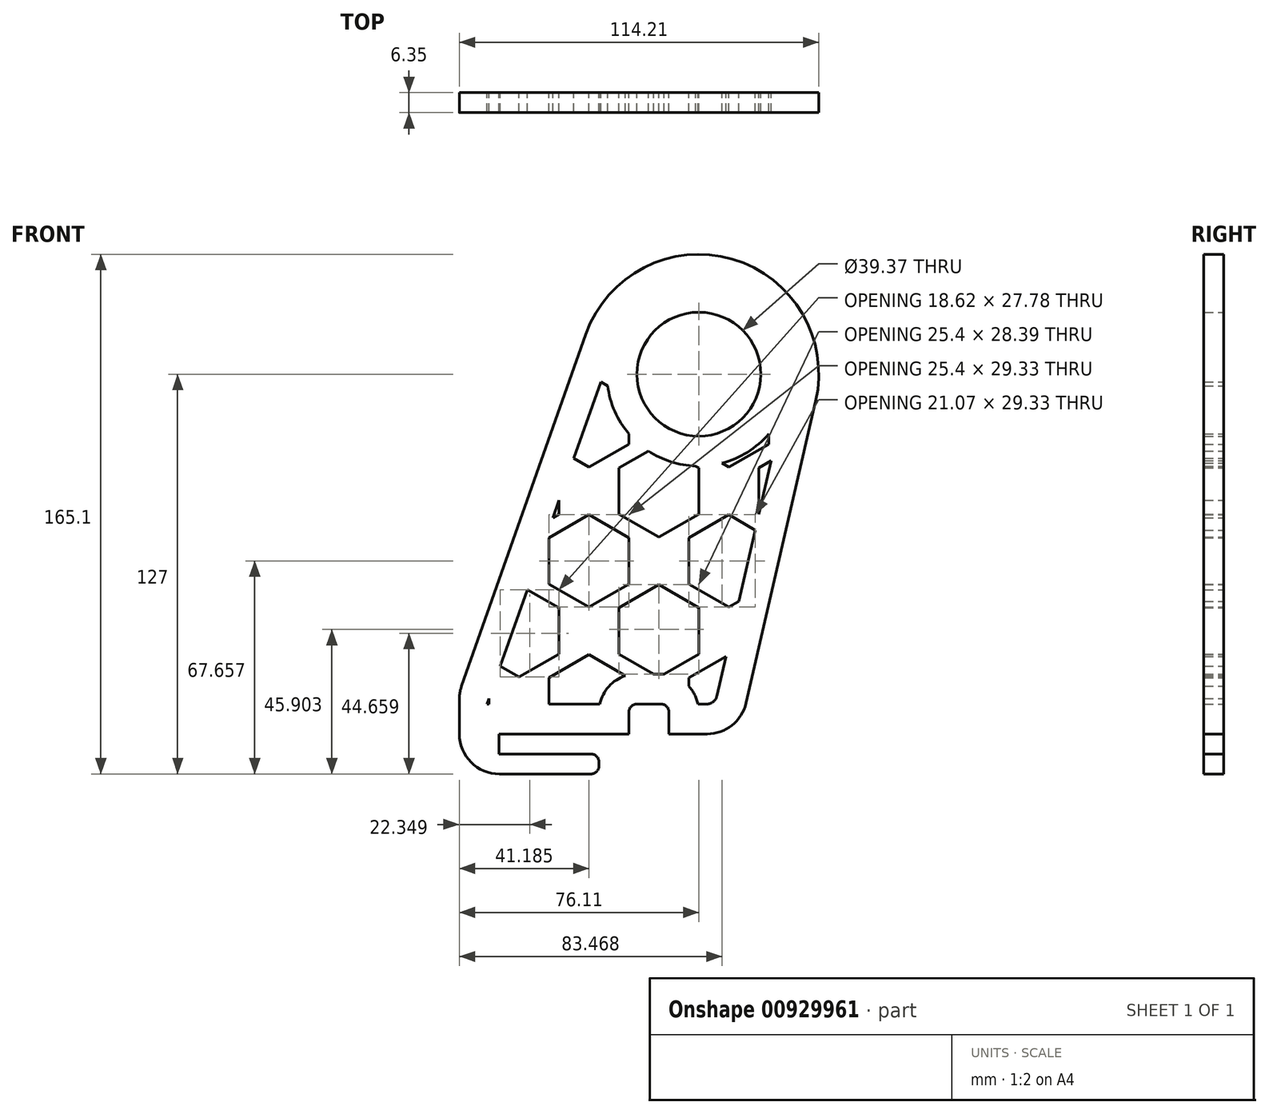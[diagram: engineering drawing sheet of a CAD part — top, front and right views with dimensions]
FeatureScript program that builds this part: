
annotation { "Feature Type Name" : "Feature", "Feature Type Description" : "" }
export const myFeature = defineFeature(function(context is Context, id is Id, definition is map)
    precondition{}
    {
        {
            var Q0;
            Q0=qCreatedBy(makeId("Front.planeOp"),FACE);
            var sketch = newSketch(context, id + "F0", { "sketchPlane" : qUnion([Q0])});
            skLineSegment(sketch, "E0", {"start": v(0, 0) * mm, "end": v(41.27, 0) * mm});
            skLineSegment(sketch, "E1", {"start": v(41.27, 0) * mm, "end": v(41.27, 9.52) * mm});
            skLineSegment(sketch, "E2", {"start": v(0, 0) * mm, "end": v(0, -6.35) * mm});
            skLineSegment(sketch, "E3", {"start": v(0, -6.35) * mm, "end": v(31.75, -6.35) * mm});
            skLineSegment(sketch, "E4", {"start": v(31.75, -6.35) * mm, "end": v(31.75, -12.7) * mm});
            skLineSegment(sketch, "E5", {"start": v(31.75, -12.7) * mm, "end": v(-12.6, -12.7) * mm});
            skLineSegment(sketch, "E6", {"start": v(-12.6, -12.7) * mm, "end": v(-12.6, 13.18) * mm});
            skLineSegment(sketch, "E7", {"start": v(41.27, 9.52) * mm, "end": v(53.98, 9.52) * mm});
            skLineSegment(sketch, "E8", {"start": v(53.98, 9.53) * mm, "end": v(53.98, 0) * mm});
            skLineSegment(sketch, "E9", {"start": v(53.98, 0) * mm, "end": v(76.2, 0) * mm});
            skCircle(sketch, "E10", {"center": v(63.5, 114.3) * mm, "radius": 19.69 * mm});
            skArc(sketch, "E11", {"start": v(100.62, 105.72) * mm, "mid": v(74.15, 150.88) * mm, "end": v(27.57, 126.98) * mm});
            skLineSegment(sketch, "E12", {"start": v(-12.6, 13.18) * mm, "end": v(27.57, 126.98) * mm});
            skLineSegment(sketch, "E13", {"start": v(76.2, 0) * mm, "end": v(100.62, 105.72) * mm});
            skSolve(sketch);
        }
        {
            var Q0;
            Q0=makeQuery(id+"F0.imprint","IMPRINT",FACE,{"disambiguationData":[TD([[makeQuery(id+"F0.imprint","IMPRINT",EDGE,{"derivedFrom":sQuery(id+"F0.wireOp",EDGE,"E0")}),1.0]])]});
            var Q1;
            Q1 = qSketchRegion(id + "F0", true);
            extrude(context, id + "F1", {"entities" : qUnion([Q0, Q1]), "depth" : 6.35 * mm, "offsetDistance" : 25.4 * mm});
        }
        {
            var Q0;
            Q0=makeQuery(id+"F1.opExtrude","SWEPT_EDGE",EDGE,{"disambiguationData":[OSD([sQuery(id+"F0.wireOp",EDGE,"E3"),sQuery(id+"F0.wireOp",EDGE,"E4")])]});
            var Q1;
            Q1=makeQuery(id+"F1.opExtrude","SWEPT_EDGE",EDGE,{"disambiguationData":[OSD([sQuery(id+"F0.wireOp",EDGE,"E4"),sQuery(id+"F0.wireOp",EDGE,"E5")])]});
            var Q2;
            Q2=makeQuery(id+"F1.opExtrude","SWEPT_EDGE",EDGE,{"disambiguationData":[OSD([sQuery(id+"F0.wireOp",EDGE,"E1"),sQuery(id+"F0.wireOp",EDGE,"E7")])]});
            var Q3;
            Q3=makeQuery(id+"F1.opExtrude","SWEPT_EDGE",EDGE,{"disambiguationData":[OSD([sQuery(id+"F0.wireOp",EDGE,"E7"),sQuery(id+"F0.wireOp",EDGE,"E8")])]});
            fillet(context, id + "F2", {"entities" : qUnion([Q0, Q1, Q2, Q3]), "radius" : 2.54 * mm, "tangentPropagation" : true, "allowEdgeOverflow" : false});
        }
        {
            var Q0;
            Q0=makeQuery(id+"F1.opExtrude","SWEPT_EDGE",EDGE,{"disambiguationData":[OSD([sQuery(id+"F0.wireOp",EDGE,"E5"),sQuery(id+"F0.wireOp",EDGE,"E6")])]});
            var Q1;
            Q1=makeQuery(id+"F1.opExtrude","SWEPT_EDGE",EDGE,{"disambiguationData":[OSD([sQuery(id+"F0.wireOp",EDGE,"E6"),sQuery(id+"F0.wireOp",EDGE,"E12")])]});
            var Q2;
            Q2=makeQuery(id+"F1.opExtrude","SWEPT_EDGE",EDGE,{"disambiguationData":[OSD([sQuery(id+"F0.wireOp",EDGE,"E9"),sQuery(id+"F0.wireOp",EDGE,"E13")])]});
            fillet(context, id + "F3", {"entities" : qUnion([Q0, Q1, Q2]), "radius" : 12.7 * mm, "tangentPropagation" : true, "allowEdgeOverflow" : false});
        }
        {
            var Q0;
            Q0=qCreatedBy(makeId("Front.planeOp"),FACE);
            var sketch = newSketch(context, id + "F4", { "sketchPlane" : qUnion([Q0])});
            skLineSegment(sketch, "E14.0", {"start": v(-11.88, 15.23) * mm, "end": v(27.57, 126.98) * mm, "construction": true});
            skArc(sketch, "E15.0", {"start": v(100.62, 105.72) * mm, "mid": v(74.15, 150.88) * mm, "end": v(27.57, 126.98) * mm, "construction": true});
            skLineSegment(sketch, "E16.0", {"start": v(78.47, 9.84) * mm, "end": v(100.62, 105.72) * mm, "construction": true});
            skArc(sketch, "E17.0", {"start": v(66.1, 0) * mm, "mid": v(74, 2.76) * mm, "end": v(78.47, 9.84) * mm, "construction": true});
            skLineSegment(sketch, "E18.0", {"start": v(53.98, 0) * mm, "end": v(66.1, 0) * mm, "construction": true});
            skLineSegment(sketch, "E19.0", {"start": v(53.98, 6.98) * mm, "end": v(53.98, 0) * mm, "construction": true});
            skArc(sketch, "E20.0", {"start": v(51.44, 9.52) * mm, "mid": v(53.23, 8.78) * mm, "end": v(53.98, 6.98) * mm, "construction": true});
            skLineSegment(sketch, "E21.0", {"start": v(43.81, 9.52) * mm, "end": v(51.44, 9.52) * mm, "construction": true});
            skArc(sketch, "E22.0", {"start": v(41.27, 6.98) * mm, "mid": v(42.02, 8.78) * mm, "end": v(43.81, 9.52) * mm, "construction": true});
            skLineSegment(sketch, "E23.0", {"start": v(41.27, 0) * mm, "end": v(41.27, 6.98) * mm, "construction": true});
            skLineSegment(sketch, "E24.0", {"start": v(0, 0) * mm, "end": v(41.27, 0) * mm, "construction": true});
            skCircle(sketch, "E25.0", {"center": v(63.5, 114.3) * mm, "radius": 19.68 * mm, "construction": true});
            skArc(sketch, "E26.0", {"start": v(34.52, 110.64) * mm, "mid": v(36.78, 102.5) * mm, "end": v(41.27, 95.35) * mm});
            skLineSegment(sketch, "E27.0", {"start": v(-3.8, 9.53) * mm, "end": v(-3.18, 9.53) * mm});
            skArc(sketch, "E27.1", {"start": v(66.1, 9.53) * mm, "mid": v(68.08, 10.22) * mm, "end": v(69.2, 11.99) * mm});
            skLineSegment(sketch, "E27.2", {"start": v(69.2, 11.99) * mm, "end": v(72.12, 24.65) * mm});
            skLineSegment(sketch, "E27.4", {"start": v(-3.8, 9.52) * mm, "end": v(-3.18, 11.28) * mm});
            skLineSegment(sketch, "E27.5", {"start": v(63.23, 9.53) * mm, "end": v(66.1, 9.53) * mm});
            skArc(sketch, "E27.7", {"start": v(51.44, 19.05) * mm, "mid": v(51.93, 19.04) * mm, "end": v(52.43, 19) * mm});
            skLineSegment(sketch, "E27.8", {"start": v(49.1, 19.05) * mm, "end": v(51.44, 19.05) * mm});
            skArc(sketch, "E27.9", {"start": v(32.02, 9.53) * mm, "mid": v(34.89, 15.1) * mm, "end": v(40.16, 18.48) * mm});
            skLineSegment(sketch, "E28.1.0.1", {"start": v(9.03, 45.85) * mm, "end": v(19.05, 40.06) * mm});
            skPoint(sketch, "E28.1.0.2", {"position": v(19.05, 32.73) * mm});
            skLineSegment(sketch, "E28.1.0.3", {"start": v(6.35, 18.07) * mm, "end": v(0.43, 21.49) * mm});
            skLineSegment(sketch, "E28.1.0.5", {"start": v(19.05, 40.06) * mm, "end": v(19.05, 25.4) * mm});
            skLineSegment(sketch, "E28.1.0.6", {"start": v(19.05, 25.4) * mm, "end": v(6.35, 18.07) * mm});
            skLineSegment(sketch, "E28.1.1.5", {"start": v(19.05, 74.23) * mm, "end": v(19.05, 69.85) * mm});
            skLineSegment(sketch, "E28.1.1.6", {"start": v(19.05, 69.85) * mm, "end": v(17.1, 68.73) * mm});
            skLineSegment(sketch, "E28.2.0.1", {"start": v(50.8, 47.4) * mm, "end": v(63.5, 40.06) * mm});
            skPoint(sketch, "E28.2.0.2", {"position": v(63.5, 32.73) * mm});
            skLineSegment(sketch, "E28.2.0.3", {"start": v(49.1, 19.05) * mm, "end": v(38.1, 25.4) * mm});
            skLineSegment(sketch, "E28.2.0.4", {"start": v(38.1, 40.06) * mm, "end": v(50.8, 47.4) * mm});
            skLineSegment(sketch, "E28.2.0.5", {"start": v(63.5, 40.06) * mm, "end": v(63.5, 25.4) * mm});
            skLineSegment(sketch, "E28.2.0.6", {"start": v(63.5, 25.4) * mm, "end": v(52.43, 19) * mm});
            skLineSegment(sketch, "E28.2.0.7", {"start": v(38.1, 25.4) * mm, "end": v(38.1, 40.06) * mm});
            skLineSegment(sketch, "E28.2.1.1", {"start": v(62.47, 85.1) * mm, "end": v(63.5, 84.51) * mm});
            skPoint(sketch, "E28.2.1.2", {"position": v(63.5, 77.18) * mm});
            skLineSegment(sketch, "E28.2.1.3", {"start": v(50.8, 62.52) * mm, "end": v(38.1, 69.85) * mm});
            skLineSegment(sketch, "E28.2.1.4", {"start": v(38.1, 84.51) * mm, "end": v(47.44, 89.9) * mm});
            skLineSegment(sketch, "E28.2.1.5", {"start": v(63.5, 84.51) * mm, "end": v(63.5, 69.85) * mm});
            skLineSegment(sketch, "E28.2.1.6", {"start": v(63.5, 69.85) * mm, "end": v(50.8, 62.52) * mm});
            skLineSegment(sketch, "E28.2.1.7", {"start": v(38.1, 69.85) * mm, "end": v(38.1, 84.51) * mm});
            skLineSegment(sketch, "E28.3.1.4", {"start": v(82.55, 84.51) * mm, "end": v(86.47, 86.78) * mm});
            skLineSegment(sketch, "E28.3.1.7", {"start": v(82.55, 69.85) * mm, "end": v(82.55, 84.51) * mm});
            skLineSegment(sketch, "E29.0", {"start": v(-3.18, 11.28) * mm, "end": v(-3.18, 9.53) * mm});
            skLineSegment(sketch, "E30.1.0.0", {"start": v(15.88, 9.53) * mm, "end": v(15.88, 17.84) * mm});
            skLineSegment(sketch, "E30.1.0.1", {"start": v(15.88, 17.84) * mm, "end": v(28.58, 25.17) * mm});
            skPoint(sketch, "E30.1.0.5", {"position": v(41.27, 10.5) * mm});
            skLineSegment(sketch, "E30.1.0.7", {"start": v(28.58, 25.17) * mm, "end": v(40.16, 18.48) * mm});
            skLineSegment(sketch, "E30.1.1.0", {"start": v(15.88, 47.63) * mm, "end": v(15.88, 62.29) * mm});
            skLineSegment(sketch, "E30.1.1.1", {"start": v(15.88, 62.29) * mm, "end": v(28.58, 69.62) * mm});
            skLineSegment(sketch, "E30.1.1.2", {"start": v(28.58, 40.3) * mm, "end": v(15.88, 47.62) * mm});
            skLineSegment(sketch, "E30.1.1.3", {"start": v(41.28, 47.62) * mm, "end": v(28.58, 40.3) * mm});
            skLineSegment(sketch, "E30.1.1.4", {"start": v(41.27, 62.29) * mm, "end": v(41.27, 47.63) * mm});
            skPoint(sketch, "E30.1.1.5", {"position": v(41.27, 54.96) * mm});
            skLineSegment(sketch, "E30.1.1.7", {"start": v(28.58, 69.62) * mm, "end": v(41.27, 62.29) * mm});
            skLineSegment(sketch, "E30.1.2.2", {"start": v(28.58, 84.74) * mm, "end": v(23.75, 87.53) * mm});
            skLineSegment(sketch, "E30.1.2.3", {"start": v(41.28, 92.07) * mm, "end": v(28.58, 84.74) * mm});
            skLineSegment(sketch, "E30.1.2.4", {"start": v(41.27, 95.35) * mm, "end": v(41.28, 92.08) * mm});
            skLineSegment(sketch, "E30.1.2.7", {"start": v(32.35, 111.9) * mm, "end": v(34.52, 110.64) * mm});
            skLineSegment(sketch, "E30.2.0.0", {"start": v(60.33, 15.14) * mm, "end": v(60.33, 17.84) * mm});
            skLineSegment(sketch, "E30.2.0.1", {"start": v(60.33, 17.84) * mm, "end": v(72.12, 24.65) * mm});
            skLineSegment(sketch, "E30.2.1.0", {"start": v(60.33, 47.62) * mm, "end": v(60.33, 62.29) * mm});
            skLineSegment(sketch, "E30.2.1.1", {"start": v(60.33, 62.29) * mm, "end": v(73.03, 69.62) * mm});
            skLineSegment(sketch, "E30.2.1.2", {"start": v(73.03, 40.3) * mm, "end": v(60.33, 47.62) * mm});
            skLineSegment(sketch, "E30.2.1.3", {"start": v(76.15, 42.1) * mm, "end": v(73.03, 40.3) * mm});
            skLineSegment(sketch, "E30.2.1.7", {"start": v(73.03, 69.62) * mm, "end": v(81.4, 64.8) * mm});
            skLineSegment(sketch, "E30.2.2.2", {"start": v(73.03, 84.74) * mm, "end": v(70.81, 86.02) * mm});
            skLineSegment(sketch, "E30.2.2.3", {"start": v(85.73, 92.08) * mm, "end": v(73.03, 84.74) * mm});
            skLineSegment(sketch, "E30.2.2.4", {"start": v(85.73, 95.35) * mm, "end": v(85.73, 92.08) * mm});
            skLineSegment(sketch, "E31.trimOffspring", {"start": v(82.56, 69.85) * mm, "end": v(82.55, 69.85) * mm});
            skArc(sketch, "E32.trimOffspring", {"start": v(47.44, 89.9) * mm, "mid": v(54.62, 86.47) * mm, "end": v(62.47, 85.1) * mm});
            skArc(sketch, "E33.trimOffspring", {"start": v(70.81, 86.02) * mm, "mid": v(78.99, 89.53) * mm, "end": v(85.73, 95.35) * mm});
            skLineSegment(sketch, "E34.trimOffspring", {"start": v(23.75, 87.53) * mm, "end": v(32.35, 111.9) * mm});
            skLineSegment(sketch, "E35.trimOffspring", {"start": v(17.1, 68.73) * mm, "end": v(19.05, 74.23) * mm});
            skLineSegment(sketch, "E36.trimOffspring", {"start": v(0.43, 21.49) * mm, "end": v(9.03, 45.85) * mm});
            skLineSegment(sketch, "E37.trimOffspring", {"start": v(15.88, 9.53) * mm, "end": v(32.02, 9.53) * mm});
            skArc(sketch, "E38.trimOffspring", {"start": v(60.33, 15.14) * mm, "mid": v(62.15, 12.53) * mm, "end": v(63.23, 9.52) * mm});
            skLineSegment(sketch, "E39.trimOffspring", {"start": v(76.15, 42.1) * mm, "end": v(81.4, 64.8) * mm});
            skLineSegment(sketch, "E40.trimOffspring", {"start": v(82.56, 69.85) * mm, "end": v(86.47, 86.78) * mm});
            skSolve(sketch);
        }
        {
            var Q0;
            Q0 = qSketchRegion(id + "F4", true);
            extrude(context, id + "F5", {"entities" : qUnion([Q0]), "operationType" : NewBodyOperationType.REMOVE, "endBound" : BoundingType.THROUGH_ALL, "depth" : 25.4 * mm, "offsetDistance" : 25.4 * mm});
        }
    });
